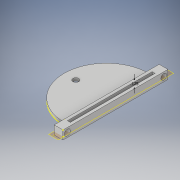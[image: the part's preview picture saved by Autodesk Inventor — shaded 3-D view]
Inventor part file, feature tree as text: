
AUTODESK INVENTOR PART (.ipt)
format: ipt  version: 2018 (Build 220112000, 112)  size: 156,160 bytes
history: native  units: in
note: dims shown in document units (in); Inventor stores cm internally (conversion verified against a paired STEP export)
features: sketch x13, extrude x5, hole x1, plane x1
ambient origin geometry x8: Origin, YZ Plane, XZ Plane, XY Plane, X Axis, Y Axis, Z Axis, Center Point
bodies: Solid1 (feature_tree)
feature tree (20):
  extrude  "Extrusion1"  Depth=4.5in
  sketch  "Sketch2"  dims[d2=0.375in d3=0.0in d4=0.25in]
  hole  "Hole1"  [1 undecoded]
  extrude  "Extrusion2"  Depth=0.25in TaperAngle=0.0deg
  extrude  "Extrusion3"  Depth=0.375in TaperAngle=0.0deg
  sketch  "Sketch6"  dims[d18=0.125in d19=90.0deg]
  sketch  "Sketch7"  dims[d20=0.125in d21=0.0in d22=0.25in]
  sketch  "Sketch8"  dims[d23=0.125in d24=0.0in]
  plane  "Work Plane1"
  sketch  "Sketch9"
  extrude  "Extrusion4"  TaperAngle=90.0deg  [1 undecoded]
  sketch  "Sketch11"
  sketch  "Sketch12"
  extrude  "Extrusion5"  Depth=0.25in
  sketch  "Sketch1"  dims[d0=0.375in d1=4.5in]
  sketch  "Sketch3"  dims[d5=0.25in]
  sketch  "Sketch4"  dims[d6=0.25in d7=0.75in d8=0.119in d9=0.25in d10=0.5635in d11=0.25in d12=0.0in d13=0.5in d14=0.0in]
  sketch  "Sketch5"  dims[d15=0.125in d16=0.375in d17=0.0in]
  sketch  "Sketch10"
  sketch  "Sketch13"
note: 2 required parameter values undecoded (feature->parameter linkage not recoverable at this tier; creation-order binding heuristic only, values carry confidence <= 0.55)
